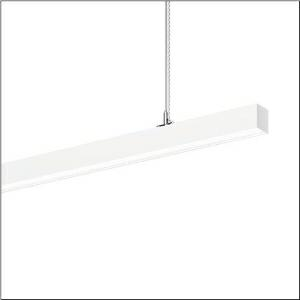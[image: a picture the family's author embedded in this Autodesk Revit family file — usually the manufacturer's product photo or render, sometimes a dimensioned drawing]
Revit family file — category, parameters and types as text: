
# Revit family: silica_21_51mx33tat7w
name_source: partatom
category: Lighting Fixtures
units: mm (PartAtom-declared; Revit-internal decimal feet)

## family parameters
Cut with Voids When Loaded = No
Host = Face
Light Source = No
Part Type = Normal
Room Calculation Point = No
Round Connector Dimension = Use Diameter
Shared = No

## types (1)
- --- (1 x LED, 5740 lm, 53.8 W, 6500K)
    Apparent Load = 54 VA
    CIE Flux Codes = 78 96 99 56 100
    Color Rendering = 80
    Color Temperature = 6500K
    Default Elevation = 1800 mm
    Description = Silica 21, office luminaire, primary optical cover: prismatic diffuser, of PMMA, CAT 2 (L<= 3000cd/m²), light emission: direct/indirect distribution, primary light characteristic: symmetric, installation type: suspended mounting, LED, rated luminous flux: 5.740lm, luminous efficacy: 102lm/W, light colour: 8tw, colour temperature: 2700..6500K, control gear: DALI DT8, with terminal, 3+2-pole, max. 2.5mm², mains connection: 220..240V, AC, 50/60Hz, rated input power: 56.5W, luminaire housing, of aluminium, traffic white (RAL 9016), length: 1.204mm, width: 53mm, height: 53mm, protection rating (complete): IP20, insulation class (complete): insulation class I (protective earthing), certification: CE, permissible operating ambient temperature: 0..+35°C, standard: EN 50419, packaging unit: 1 piece
    Height = 53 mm
    Lamp = 1 x LED
    Lamp Light Flux = 5740 lm
    Lamp Power = 53.8 W
    Lamp count = 1
    Length = 1204 mm
    Luminous efficacy = 107 lm/W
    Manufacturer = Siteco
    ModVariant = No
    Model = 51MX33TAT7W
    Mounting Place = Ceiling
    Mounting Type = Pendant
    Number of Poles = 1
    OnlyDefault = Yes
    Power Factor = 1
    Product Name = Silica 21
    Product group = office luminaire | ceiling pendant
    ProductGroupID = 903
    Protection Class = Protection class I
    Protection Degree = IP 20
    RLX_Detail_Level = 1
    RLX_Emergency_Light_Flux = 0 lm
    RLX_Emergency_Type = 0
    RLX_Emergency_Type_DB = No
    RlxData = <blob elided: 18169 chars, md5=ae001301>
    Socket = socket
    Standby Power = 0 W
    System Light Flux = 5740 lm
    System Power = 54 W
    Type Comments = individual setting
    Type Image = l_1349007.jpg
    URL = http://relux.com
    VarID = @adj_139277
    Voltage = 0 V
    Weight = 0.00 kg
    Width = 53 mm

## geometry (parser evidence)
native form markers: Blend x4, Sweep x13
no freeform markers — native parametric forms only
